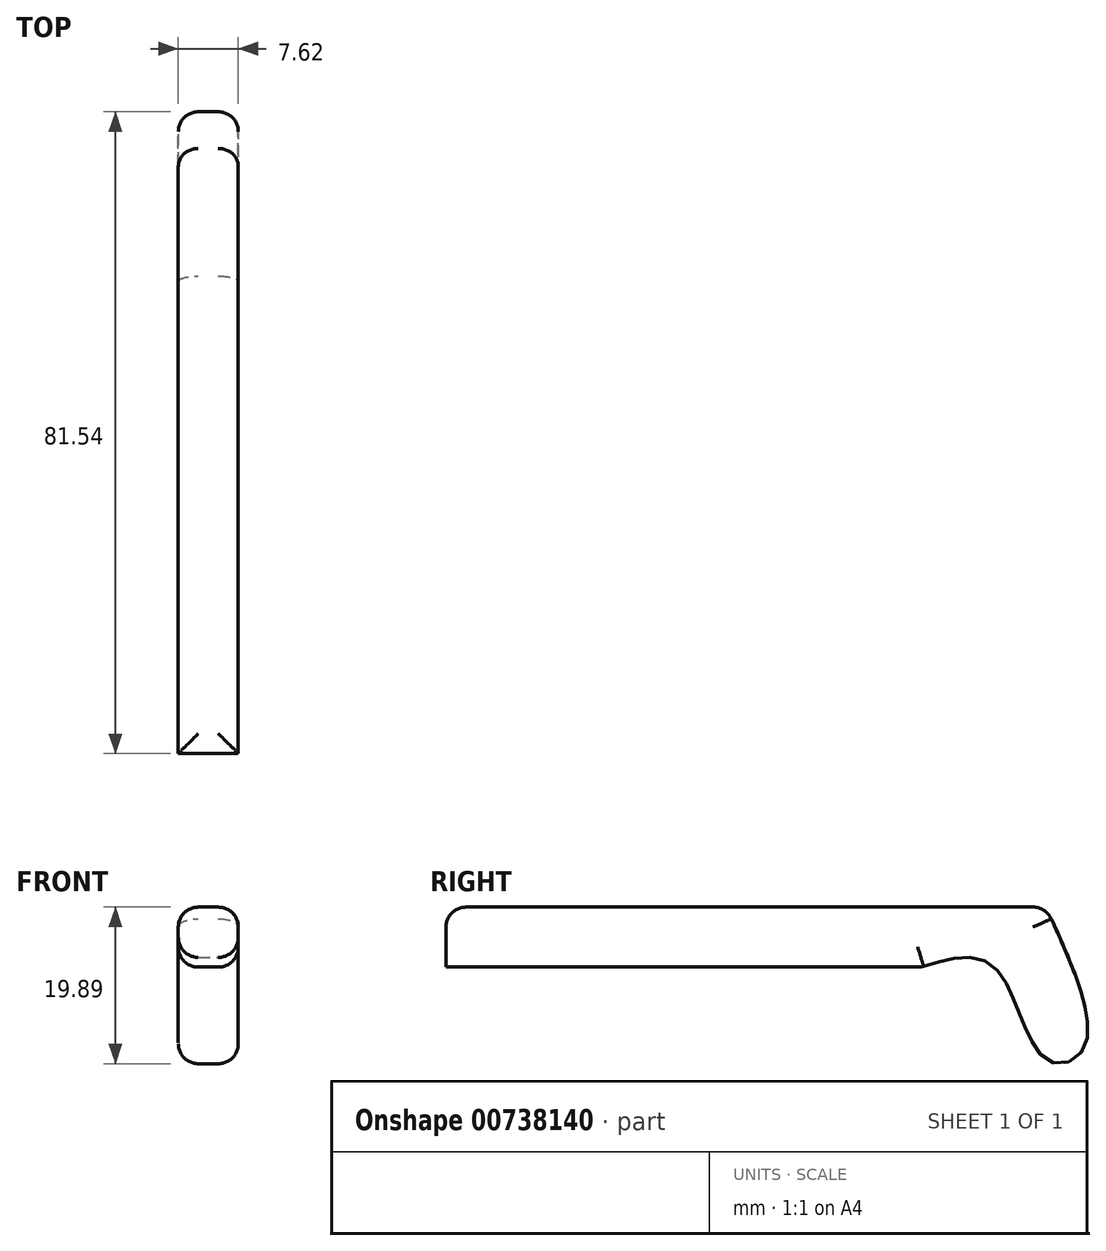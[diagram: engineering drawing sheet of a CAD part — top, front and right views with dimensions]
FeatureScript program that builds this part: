
annotation { "Feature Type Name" : "Feature", "Feature Type Description" : "" }
export const myFeature = defineFeature(function(context is Context, id is Id, definition is map)
    precondition{}
    {
        {
            var Q0;
            Q0=qCreatedBy(makeId("Right.planeOp"),FACE);
            var sketch = newSketch(context, id + "F0", { "sketchPlane" : qUnion([Q0])});
            skLineSegment(sketch, "E0.0", {"start": v(0, 32.73) * mm, "end": v(0, 25.1) * mm});
            skLineSegment(sketch, "E0.1", {"start": v(0, 32.73) * mm, "end": v(0, 25.1) * mm});
            skLineSegment(sketch, "E1.bottom", {"start": v(0, 32.73) * mm, "end": v(76.2, 32.73) * mm});
            skLineSegment(sketch, "E1.top", {"start": v(0, 25.1) * mm, "end": v(60.3, 25.1) * mm});
            skFitSpline(sketch, "E2", {"points": [v(76.2, 32.73) * mm, v(81.06, 14.89) * mm, v(76.2, 13.39) * mm, v(69.63, 25.1) * mm, v(60.3, 25.1) * mm], "startDerivative": vector(30.52, -66.35) * mm, "endDerivative": vector(-45.7, -14.02) * mm});
            skSolve(sketch);
        }
        {
            var Q0;
            Q0=makeQuery(id+"F0.imprint","IMPRINT",FACE,{"disambiguationData":[TD([[makeQuery(id+"F0.imprint","IMPRINT",EDGE,{"derivedFrom":sQuery(id+"F0.wireOp",EDGE,"E1.bottom")}),-1.0]])]});
            extrude(context, id + "F1", {"entities" : qUnion([Q0]), "oppositeDirection" : true, "depth" : 7.62 * mm, "offsetDistance" : 25.4 * mm});
        }
        {
            var Q0;
            Q0=makeQuery(id+"F1.opExtrude","CAP_EDGE",EDGE,{"disambiguationData":[OSD([sQuery(id+"F0.wireOp",EDGE,"E2")])],"isStart":false});
            var Q1;
            Q1=makeQuery(id+"F1.opExtrude","SWEPT_EDGE",EDGE,{"disambiguationData":[OSD([sQuery(id+"F0.wireOp",EDGE,"E1.bottom"),sQuery(id+"F0.wireOp",EDGE,"E2")])]});
            var Q2;
            Q2=makeQuery(id+"F1.opExtrude","CAP_EDGE",EDGE,{"disambiguationData":[OSD([sQuery(id+"F0.wireOp",EDGE,"E2")])],"isStart":true});
            fillet(context, id + "F2", {"entities" : qUnion([Q0, Q1, Q2]), "radius" : 2.54 * mm, "tangentPropagation" : true, "allowEdgeOverflow" : false});
        }
        {
            var Q0;
            Q0=makeQuery(id+"F1.opExtrude","SWEPT_FACE",FACE,{"disambiguationData":[OSD([sQuery(id+"F0.wireOp",EDGE,"E1.bottom")])]});
            fillet(context, id + "F3", {"entities" : qUnion([Q0]), "radius" : 2.54 * mm, "tangentPropagation" : true, "allowEdgeOverflow" : false});
        }
        {
            var Q0;
            Q0=makeQuery(id+"F1.opExtrude","CAP_EDGE",EDGE,{"disambiguationData":[OSD([sQuery(id+"F0.wireOp",EDGE,"E1.top")])],"isStart":true});
            fillet(context, id + "F4", {"entities" : qUnion([Q0]), "radius" : 2.54 * mm, "tangentPropagation" : true, "allowEdgeOverflow" : false});
        }
    });
